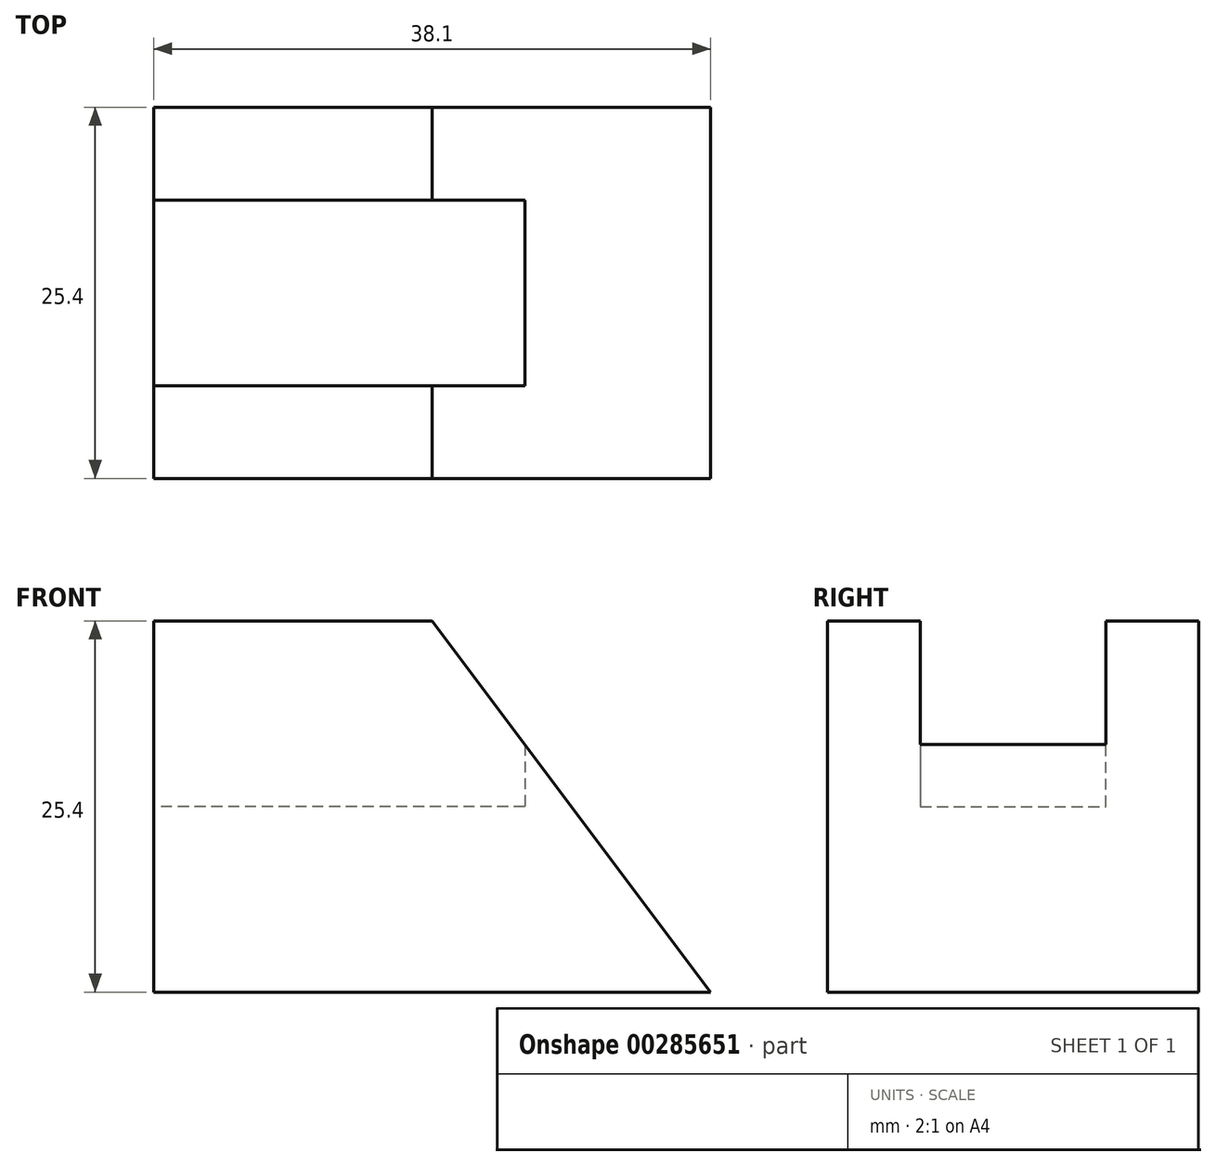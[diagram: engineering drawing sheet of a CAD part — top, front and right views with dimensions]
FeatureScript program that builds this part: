
annotation { "Feature Type Name" : "Feature", "Feature Type Description" : "" }
export const myFeature = defineFeature(function(context is Context, id is Id, definition is map)
    precondition{}
    {
        {
            var Q0;
            Q0=qCreatedBy(makeId("Front.planeOp"),FACE);
            var sketch = newSketch(context, id + "F0", { "sketchPlane" : qUnion([Q0])});
            skLineSegment(sketch, "E0", {"start": v(0, 0) * mm, "end": v(0, 25.4) * mm});
            skLineSegment(sketch, "E1", {"start": v(0, 25.4) * mm, "end": v(19.05, 25.4) * mm});
            skLineSegment(sketch, "E2", {"start": v(19.05, 25.4) * mm, "end": v(38.1, 0) * mm});
            skLineSegment(sketch, "E3", {"start": v(38.1, 0) * mm, "end": v(0, 0) * mm});
            skSolve(sketch);
        }
        {
            var Q0;
            Q0 = qSketchRegion(id + "F0", true);
            extrude(context, id + "F1", {"entities" : qUnion([Q0]), "depth" : 25.4 * mm});
        }
        {
            var Q0;
            Q0=qCreatedBy(makeId("Right.planeOp"),FACE);
            var sketch = newSketch(context, id + "F2", { "sketchPlane" : qUnion([Q0])});
            skLineSegment(sketch, "E4", {"start": v(-19.05, 25.4) * mm, "end": v(-19.05, 12.7) * mm});
            skLineSegment(sketch, "E5", {"start": v(-19.05, 12.7) * mm, "end": v(-6.35, 12.7) * mm});
            skLineSegment(sketch, "E6", {"start": v(-6.35, 12.7) * mm, "end": v(-6.35, 25.4) * mm});
            skLineSegment(sketch, "E7", {"start": v(-6.35, 25.4) * mm, "end": v(-19.05, 25.4) * mm});
            skSolve(sketch);
        }
        {
            var Q0;
            Q0 = qSketchRegion(id + "F2", true);
            extrude(context, id + "F3", {"entities" : qUnion([Q0]), "operationType" : NewBodyOperationType.REMOVE, "depth" : 25.4 * mm});
        }
    });
